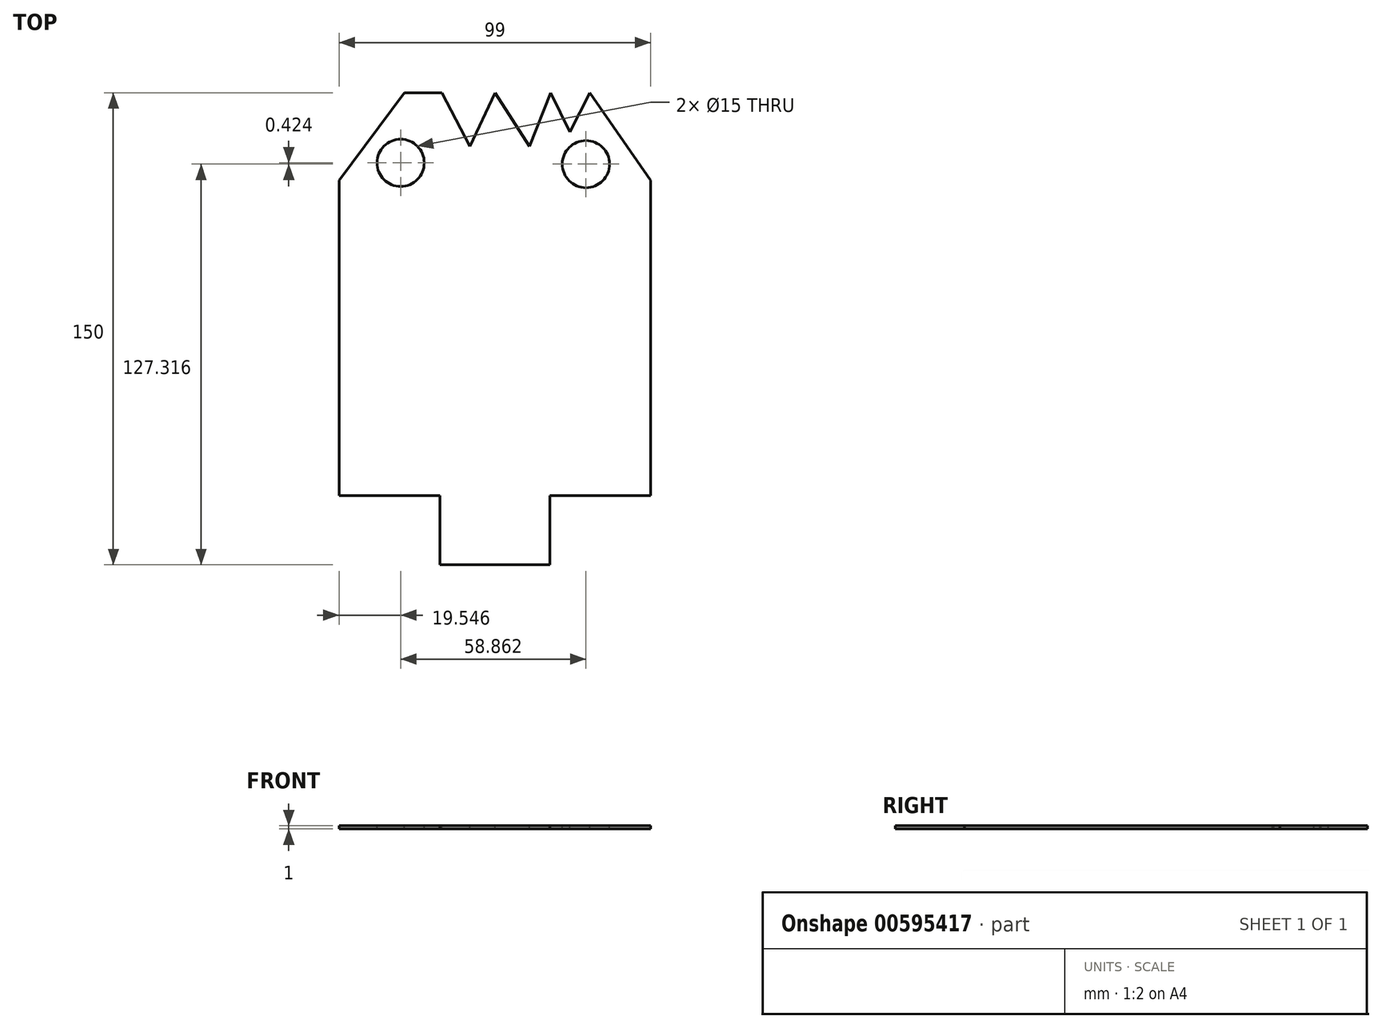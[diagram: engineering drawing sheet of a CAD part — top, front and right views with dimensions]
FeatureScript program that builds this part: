
annotation { "Feature Type Name" : "Feature", "Feature Type Description" : "" }
export const myFeature = defineFeature(function(context is Context, id is Id, definition is map)
    precondition{}
    {
        {
            var Q0;
            Q0=qCreatedBy(makeId("Top.planeOp"),FACE);
            var sketch = newSketch(context, id + "F0", { "sketchPlane" : qUnion([Q0])});
            skLineSegment(sketch, "E0.bottom", {"start": v(49.5, 75) * mm, "end": v(-49.5, 75) * mm});
            skLineSegment(sketch, "E0.top", {"start": v(49.5, -75) * mm, "end": v(-49.5, -75) * mm});
            skLineSegment(sketch, "E0.left", {"start": v(49.5, 75) * mm, "end": v(49.5, -75) * mm});
            skLineSegment(sketch, "E0.right", {"start": v(-49.5, 75) * mm, "end": v(-49.5, -75) * mm});
            skPoint(sketch, "E0.middle", {"position": v(0, 0) * mm});
            skSolve(sketch);
        }
        {
            var Q0;
            Q0=makeQuery(id+"F0.imprint","IMPRINT",FACE,{"disambiguationData":[TD([[makeQuery(id+"F0.imprint","IMPRINT",EDGE,{"derivedFrom":sQuery(id+"F0.wireOp",EDGE,"E0.bottom")}),1.0]])]});
            extrude(context, id + "F1", {"entities" : qUnion([Q0]), "depth" : 1 * mm, "offsetDistance" : 25 * mm});
        }
        {
            var Q0;
            Q0=makeQuery(id+"F1.opExtrude","CAP_FACE",FACE,{"disambiguationData":[OSD([sQuery(id+"F0.wireOp",EDGE,"E0.bottom"),sQuery(id+"F0.wireOp",EDGE,"E0.top"),sQuery(id+"F0.wireOp",EDGE,"E0.left"),sQuery(id+"F0.wireOp",EDGE,"E0.right")])],"isStart":false});
            var sketch = newSketch(context, id + "F2", { "sketchPlane" : qUnion([Q0])});
            skLineSegment(sketch, "E1", {"start": v(49.5, 47.22) * mm, "end": v(30.12, 75) * mm});
            skLineSegment(sketch, "E2", {"start": v(-49.5, 47.22) * mm, "end": v(-28.74, 75) * mm});
            skCircle(sketch, "E3", {"center": v(-29.95, 52.74) * mm, "radius": 7.5 * mm});
            skCircle(sketch, "E4", {"center": v(28.9, 52.32) * mm, "radius": 7.5 * mm});
            skLineSegment(sketch, "E5", {"start": v(-49.5, -53) * mm, "end": v(-17.5, -53) * mm});
            skLineSegment(sketch, "E6", {"start": v(-17.5, -53) * mm, "end": v(-17.5, -75) * mm});
            skLineSegment(sketch, "E7", {"start": v(17.5, -75) * mm, "end": v(17.5, -53) * mm});
            skLineSegment(sketch, "E8", {"start": v(17.5, -53) * mm, "end": v(49.5, -53) * mm});
            skPoint(sketch, "E9.start.orphan", {"position": v(-7.98, 58) * mm});
            skPoint(sketch, "E10.start.orphan", {"position": v(0, 75) * mm});
            skPoint(sketch, "E11.start.orphan", {"position": v(10.96, 58) * mm});
            skLineSegment(sketch, "E12", {"start": v(-16.78, 75) * mm, "end": v(-7.98, 58) * mm});
            skLineSegment(sketch, "E13", {"start": v(-7.98, 58) * mm, "end": v(0, 75) * mm});
            skLineSegment(sketch, "E14", {"start": v(0, 75) * mm, "end": v(10.96, 58) * mm});
            skLineSegment(sketch, "E15", {"start": v(10.96, 58) * mm, "end": v(17.68, 75) * mm});
            skLineSegment(sketch, "E16", {"start": v(17.68, 75) * mm, "end": v(23.86, 62.49) * mm});
            skLineSegment(sketch, "E17", {"start": v(23.86, 62.49) * mm, "end": v(30.12, 75) * mm});
            skSolve(sketch);
        }
        {
            var Q0;
            {var subQ0=sQuery(id+"F2.wireOp",EDGE,"E1");Q0=makeQuery(id+"F2.imprint","IMPRINT",FACE,{"disambiguationData":[TD([[makeQuery(id+"F2.imprint","IMPRINT",EDGE,{"derivedFrom":subQ0}),-1.0]])]});}
            var Q1;
            {var subQ0=sQuery(id+"F2.wireOp",EDGE,"E2");Q1=makeQuery(id+"F2.imprint","IMPRINT",FACE,{"disambiguationData":[TD([[makeQuery(id+"F2.imprint","IMPRINT",EDGE,{"derivedFrom":subQ0}),1.0]])]});}
            var Q2;
            {var subQ0=sQuery(id+"F2.wireOp",EDGE,"E14");Q2=makeQuery(id+"F2.imprint","IMPRINT",FACE,{"disambiguationData":[TD([[makeQuery(id+"F2.imprint","IMPRINT",EDGE,{"derivedFrom":subQ0}),1.0]])]});}
            var Q3;
            {var subQ0=sQuery(id+"F2.wireOp",EDGE,"E16");Q3=makeQuery(id+"F2.imprint","IMPRINT",FACE,{"disambiguationData":[TD([[makeQuery(id+"F2.imprint","IMPRINT",EDGE,{"derivedFrom":subQ0}),1.0]])]});}
            var Q4;
            {var subQ0=sQuery(id+"F2.wireOp",EDGE,"E12");Q4=makeQuery(id+"F2.imprint","IMPRINT",FACE,{"disambiguationData":[TD([[makeQuery(id+"F2.imprint","IMPRINT",EDGE,{"derivedFrom":subQ0}),1.0]])]});}
            var Q5;
            Q5=sQuery(id+"F2.wireOp",EDGE,"E2");
            var Q6;
            Q6=sQuery(id+"F2.wireOp",EDGE,"E1");
            extrude(context, id + "F3", {"entities" : qUnion([Q0, Q1, Q2, Q3, Q4]), "operationType" : NewBodyOperationType.REMOVE, "surfaceEntities" : qUnion([Q5, Q6]), "oppositeDirection" : true, "depth" : 25 * mm, "offsetDistance" : 25 * mm});
        }
        {
            var Q0;
            Q0=makeQuery(id+"F2.imprint","IMPRINT",FACE,{"disambiguationData":[TD([[makeQuery(id+"F2.imprint","IMPRINT",EDGE,{"derivedFrom":sQuery(id+"F2.wireOp",EDGE,"E3")}),1.0]])]});
            var Q1;
            {var subQ0=sQuery(id+"F2.wireOp",EDGE,"E5");Q1=makeQuery(id+"F2.imprint","IMPRINT",FACE,{"disambiguationData":[TD([[makeQuery(id+"F2.imprint","IMPRINT",EDGE,{"derivedFrom":subQ0}),-1.0]])]});}
            var Q2;
            {var subQ0=sQuery(id+"F2.wireOp",EDGE,"E7");Q2=makeQuery(id+"F2.imprint","IMPRINT",FACE,{"disambiguationData":[TD([[makeQuery(id+"F2.imprint","IMPRINT",EDGE,{"derivedFrom":subQ0}),-1.0]])]});}
            var Q3;
            Q3=makeQuery(id+"F2.imprint","IMPRINT",FACE,{"disambiguationData":[TD([[makeQuery(id+"F2.imprint","IMPRINT",EDGE,{"derivedFrom":sQuery(id+"F2.wireOp",EDGE,"E4")}),1.0]])]});
            extrude(context, id + "F4", {"entities" : qUnion([Q0, Q1, Q2, Q3]), "operationType" : NewBodyOperationType.REMOVE, "oppositeDirection" : true, "depth" : 25 * mm, "offsetDistance" : 25 * mm});
        }
        {
            var Q0;
            {var subQ0=sQuery(id+"F2.wireOp",EDGE,"E7");Q0=makeQuery(id+"F2.imprint","IMPRINT",FACE,{"disambiguationData":[TD([[makeQuery(id+"F2.imprint","IMPRINT",EDGE,{"derivedFrom":subQ0}),-1.0]])]});}
            var Q1;
            {var subQ0=sQuery(id+"F2.wireOp",EDGE,"E5");Q1=makeQuery(id+"F2.imprint","IMPRINT",FACE,{"disambiguationData":[TD([[makeQuery(id+"F2.imprint","IMPRINT",EDGE,{"derivedFrom":subQ0}),-1.0]])]});}
            extrude(context, id + "F5", {"entities" : qUnion([Q0, Q1]), "operationType" : NewBodyOperationType.REMOVE, "oppositeDirection" : true, "depth" : 25 * mm, "offsetDistance" : 25 * mm});
        }
    });
